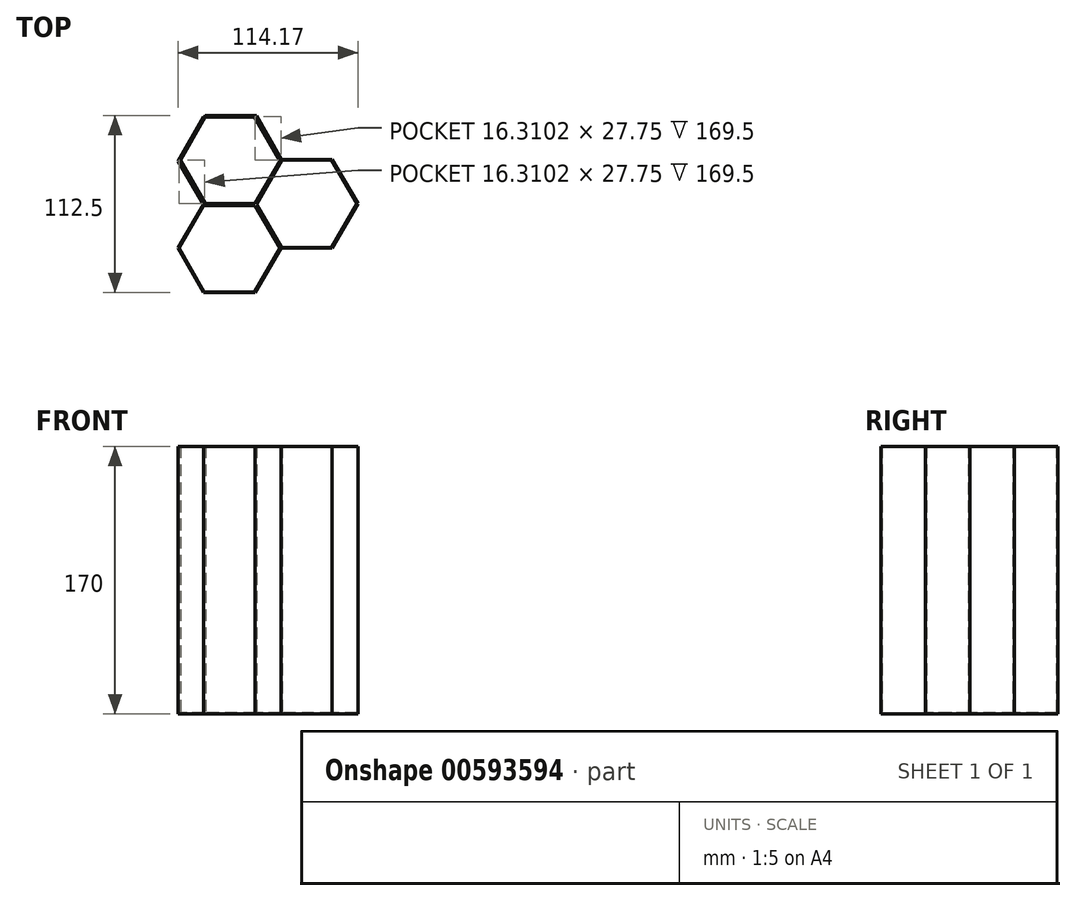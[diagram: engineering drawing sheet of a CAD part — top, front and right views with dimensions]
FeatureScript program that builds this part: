
annotation { "Feature Type Name" : "Feature", "Feature Type Description" : "" }
export const myFeature = defineFeature(function(context is Context, id is Id, definition is map)
    precondition{}
    {
        {
            var Q0;
            Q0=qCreatedBy(makeId("Top.planeOp"),FACE);
            var sketch = newSketch(context, id + "F0", { "sketchPlane" : qUnion([Q0])});
            skCircle(sketch, "E0.cCircle", {"center": v(0, 0) * mm, "radius": 28.25 * mm, "construction": true});
            skLineSegment(sketch, "E0.0", {"start": v(-16.31, 28.25) * mm, "end": v(16.31, 28.25) * mm});
            skLineSegment(sketch, "E0.1", {"start": v(16.31, 28.25) * mm, "end": v(32.62, 0) * mm});
            skLineSegment(sketch, "E0.2", {"start": v(32.62, 0) * mm, "end": v(16.31, -28.25) * mm});
            skLineSegment(sketch, "E0.3", {"start": v(16.31, -28.25) * mm, "end": v(-16.31, -28.25) * mm});
            skLineSegment(sketch, "E0.4", {"start": v(-16.31, -28.25) * mm, "end": v(-32.62, 0) * mm});
            skLineSegment(sketch, "E0.5", {"start": v(-32.62, 0) * mm, "end": v(-16.31, 28.25) * mm});
            skPoint(sketch, "E0.0.midPoint", {"position": v(0, 28.25) * mm});
            skSolve(sketch);
        }
        {
            var Q0;
            Q0=makeQuery(id+"F0.imprint","IMPRINT",FACE,{"disambiguationData":[TD([[makeQuery(id+"F0.imprint","IMPRINT",EDGE,{"derivedFrom":sQuery(id+"F0.wireOp",EDGE,"625dc4df-1560-4c75-8085-82a92da362ae.0")}),-1.0]])]});
            var Q1;
            Q1=makeQuery(id+"F0.imprint","IMPRINT",FACE,{"disambiguationData":[TD([[makeQuery(id+"F0.imprint","IMPRINT",EDGE,{"derivedFrom":sQuery(id+"F0.wireOp",EDGE,"625dc4df-1560-4c75-8085-82a92da362ae.5")}),1.0]])]});
            var Q2;
            Q2=makeQuery(id+"F0.imprint","IMPRINT",FACE,{"disambiguationData":[TD([[makeQuery(id+"F0.imprint","IMPRINT",EDGE,{"derivedFrom":sQuery(id+"F0.wireOp",EDGE,"625dc4df-1560-4c75-8085-82a92da362ae.0")}),1.0]])]});
            var Q3;
            Q3=makeQuery(id+"F0.imprint","IMPRINT",FACE,{"disambiguationData":[TD([[makeQuery(id+"F0.imprint","IMPRINT",EDGE,{"derivedFrom":sQuery(id+"F0.wireOp",EDGE,"625dc4df-1560-4c75-8085-82a92da362ae.3")}),1.0]])]});
            var Q4;
            Q4=makeQuery(id+"F0.imprint","IMPRINT",FACE,{"disambiguationData":[TD([[makeQuery(id+"F0.imprint","IMPRINT",EDGE,{"derivedFrom":sQuery(id+"F0.wireOp",EDGE,"625dc4df-1560-4c75-8085-82a92da362ae.2")}),1.0]])]});
            var Q5;
            Q5=makeQuery(id+"F0.imprint","IMPRINT",FACE,{"disambiguationData":[TD([[makeQuery(id+"F0.imprint","IMPRINT",EDGE,{"derivedFrom":sQuery(id+"F0.wireOp",EDGE,"E0.0")}),-1.0]])]});
            extrude(context, id + "F1", {"entities" : qUnion([Q0, Q1, Q2, Q3, Q4, Q5]), "depth" : 170 * mm, "offsetDistance" : 25 * mm});
        }
        {
            var Q0;
            Q0=makeQuery(id+"F1.opExtrude","CAP_FACE",FACE,{"disambiguationData":[OSD([sQuery(id+"F0.wireOp",EDGE,"E0.0"),sQuery(id+"F0.wireOp",EDGE,"E0.1"),sQuery(id+"F0.wireOp",EDGE,"E0.2"),sQuery(id+"F0.wireOp",EDGE,"E0.3"),sQuery(id+"F0.wireOp",EDGE,"E0.4"),sQuery(id+"F0.wireOp",EDGE,"E0.5")])],"isStart":false});
            shell(context, id + "F2", {"entities" : qUnion([Q0]), "thickness" : 0.5 * mm});
        }
        {
            var Q0;
            Q0=makeQuery(id+"F1.opExtrude","SWEPT_BODY",BODY,{"disambiguationData":[OSD([sQuery(id+"F0.wireOp",EDGE,"E0.0"),sQuery(id+"F0.wireOp",EDGE,"E0.1"),sQuery(id+"F0.wireOp",EDGE,"E0.2"),sQuery(id+"F0.wireOp",EDGE,"E0.3"),sQuery(id+"F0.wireOp",EDGE,"E0.4"),sQuery(id+"F0.wireOp",EDGE,"E0.5")])]});
            var Q1;
            Q1=makeQuery(id+"F2.opShell","OFFSET_FACE",FACE,{"disambiguationData":[OSD([sQuery(id+"F0.wireOp",EDGE,"E0.5")])]});
            mirror(context, id + "F3", {"operationType" : NewBodyOperationType.ADD, "entities" : qUnion([Q0]), "mirrorPlane" : qUnion([Q1])});
        }
        {
            var Q0;
            Q0=makeQuery(id+"F1.opExtrude","SWEPT_BODY",BODY,{"disambiguationData":[OSD([sQuery(id+"F0.wireOp",EDGE,"E0.0"),sQuery(id+"F0.wireOp",EDGE,"E0.1"),sQuery(id+"F0.wireOp",EDGE,"E0.2"),sQuery(id+"F0.wireOp",EDGE,"E0.3"),sQuery(id+"F0.wireOp",EDGE,"E0.4"),sQuery(id+"F0.wireOp",EDGE,"E0.5")])]});
            var Q1;
            Q1=makeQuery(id+"F3.opPattern","COPY",FACE,{"derivedFrom":makeQuery(id+"F1.opExtrude","SWEPT_FACE",FACE,{"disambiguationData":[OSD([sQuery(id+"F0.wireOp",EDGE,"E0.5")])]}),"instanceName":"1"});
            var Q2;
            Q2=makeQuery(id+"F2.opShell","OFFSET_FACE",FACE,{"disambiguationData":[OSD([sQuery(id+"F0.wireOp",EDGE,"E0.0")])]});
            var Q3;
            Q3=makeQuery(id+"F2.opShell","OFFSET_FACE",FACE,{"disambiguationData":[OSD([sQuery(id+"F0.wireOp",EDGE,"E0.1")])]});
            var Q4;
            Q4=makeQuery(id+"F1.opExtrude","SWEPT_FACE",FACE,{"disambiguationData":[OSD([sQuery(id+"F0.wireOp",EDGE,"E0.2")])]});
            var Q5;
            Q5=makeQuery(id+"F1.opExtrude","SWEPT_FACE",FACE,{"disambiguationData":[OSD([sQuery(id+"F0.wireOp",EDGE,"E0.3")])]});
            var Q6;
            Q6=makeQuery(id+"F1.opExtrude","SWEPT_FACE",FACE,{"disambiguationData":[OSD([sQuery(id+"F0.wireOp",EDGE,"E0.4")])]});
            mirror(context, id + "F4", {"operationType" : NewBodyOperationType.ADD, "entities" : qUnion([Q0]), "faces" : qUnion([Q1, Q2, Q3, Q4, Q5]), "mirrorPlane" : qUnion([Q6])});
        }
    });
